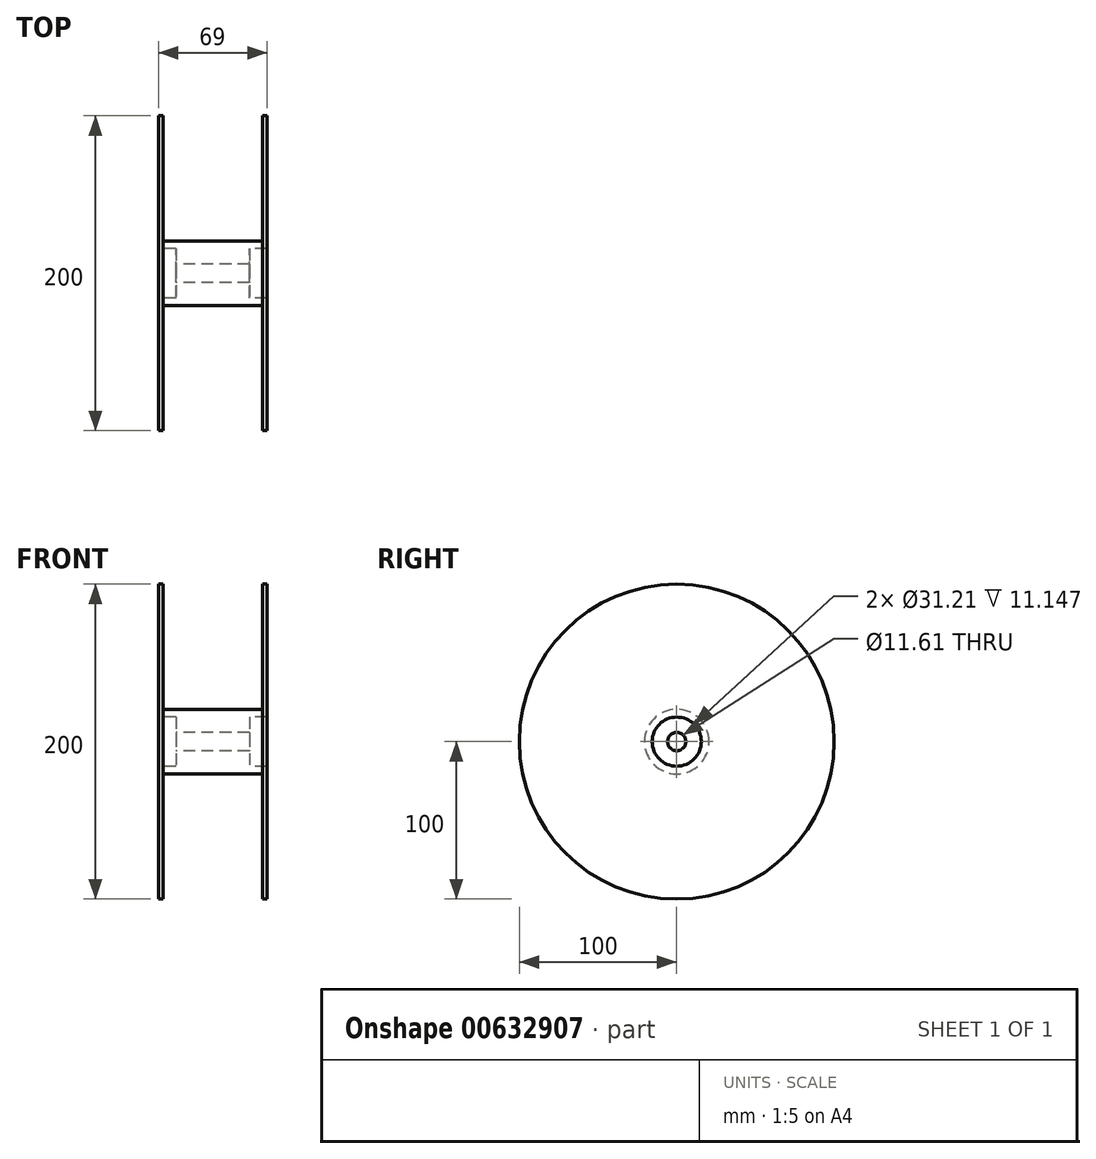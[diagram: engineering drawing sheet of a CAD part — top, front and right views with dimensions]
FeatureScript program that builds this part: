
annotation { "Feature Type Name" : "Feature", "Feature Type Description" : "" }
export const myFeature = defineFeature(function(context is Context, id is Id, definition is map)
    precondition{}
    {
        {
            var Q0;
            Q0=qCreatedBy(makeId("Front.planeOp"),FACE);
            var sketch = newSketch(context, id + "F0", { "sketchPlane" : qUnion([Q0])});
            skLineSegment(sketch, "E0", {"start": v(0, 20.55) * mm, "end": v(-31.5, 20.55) * mm});
            skLineSegment(sketch, "E1", {"start": v(-31.5, 20.55) * mm, "end": v(-31.5, 100) * mm});
            skLineSegment(sketch, "E2", {"start": v(-31.5, 100) * mm, "end": v(-34.5, 100) * mm});
            skLineSegment(sketch, "E3", {"start": v(-34.5, 100) * mm, "end": v(-34.5, 15.6) * mm});
            skLineSegment(sketch, "E4", {"start": v(-34.5, 15.6) * mm, "end": v(-23.35, 15.6) * mm});
            skLineSegment(sketch, "E5", {"start": v(-23.35, 15.6) * mm, "end": v(-23.35, 5.8) * mm});
            skLineSegment(sketch, "E6", {"start": v(-23.35, 5.8) * mm, "end": v(0, 5.8) * mm});
            skLineSegment(sketch, "E7", {"start": v(0, 20.55) * mm, "end": v(0, 5.8) * mm});
            skLineSegment(sketch, "E8.MirrorCS", {"start": v(31.5, 100) * mm, "end": v(34.5, 100) * mm});
            skLineSegment(sketch, "E9.MirrorCS", {"start": v(31.5, 20.55) * mm, "end": v(31.5, 100) * mm});
            skLineSegment(sketch, "E10.MirrorCS", {"start": v(23.35, 5.8) * mm, "end": v(0, 5.8) * mm});
            skLineSegment(sketch, "E11.MirrorCS", {"start": v(0, 20.55) * mm, "end": v(31.5, 20.55) * mm});
            skLineSegment(sketch, "E12.MirrorCS", {"start": v(23.35, 15.6) * mm, "end": v(23.35, 5.8) * mm});
            skLineSegment(sketch, "E13.MirrorCS", {"start": v(34.5, 15.6) * mm, "end": v(23.35, 15.6) * mm});
            skLineSegment(sketch, "E14.MirrorCS", {"start": v(34.5, 100) * mm, "end": v(34.5, 15.6) * mm});
            skLineSegment(sketch, "E15", {"start": v(0, 0) * mm, "end": v(13.9, 0) * mm});
            skSolve(sketch);
        }
        {
            var Q0;
            Q0=makeQuery(id+"F0.imprint","IMPRINT",FACE,{"disambiguationData":[TD([[makeQuery(id+"F0.imprint","IMPRINT",EDGE,{"derivedFrom":sQuery(id+"F0.wireOp",EDGE,"E0")}),1.0]])]});
            var Q1;
            Q1=makeQuery(id+"F0.imprint","IMPRINT",FACE,{"disambiguationData":[TD([[makeQuery(id+"F0.imprint","IMPRINT",EDGE,{"derivedFrom":sQuery(id+"F0.wireOp",EDGE,"E7")}),1.0]])]});
            var Q2;
            Q2=sQuery(id+"F0.wireOp",EDGE,"E15");
            revolve(context, id + "F1", {"entities" : qUnion([Q0, Q1]), "axis" : qUnion([Q2]), "revolveType" : RevolveType.FULL});
        }
    });
